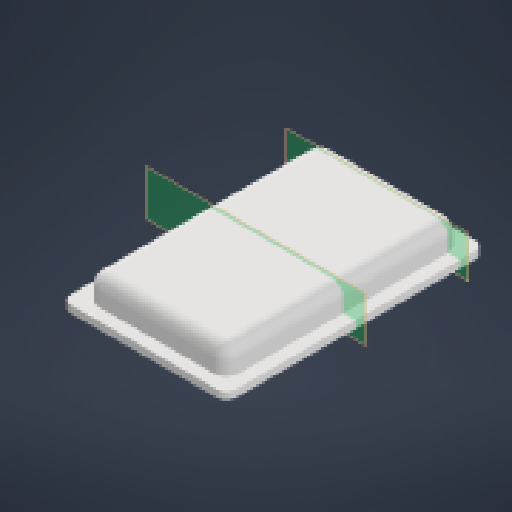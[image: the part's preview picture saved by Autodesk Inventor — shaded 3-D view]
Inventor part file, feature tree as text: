
AUTODESK INVENTOR PART (.ipt)
format: ipt  version: 2024 (Build 280153000, 153)  size: 327,168 bytes
history: native  units: mm
features: reference x17, other x6, extrude x5, sketch x5, fillet x2, chamfer x1, shell x1, mirror x1, projected_geometry x1
ambient origin geometry x8: Origin, YZ Plane, XZ Plane, XY Plane, X Axis, Y Axis, Z Axis, Center Point
bodies: Body1 (feature_tree)
feature tree (39):
  other  "Твердое тело1"
  extrude  "Выдавливание1"  Depth=2.0mm
  chamfer  "Фаска1"  Distance=2.0mm
  extrude  "Выдавливание2"  Depth=1.0mm TaperAngle=45.0deg
  extrude  "Выдавливание3"  Depth=3.0mm TaperAngle=0.0deg
  fillet  "Сопряжение1"  Radius=5.0mm
  other  "РабПлоскость1"
  other  "РабПлоскость2"
  shell  "Оболочка1"  Thickness=10.25mm
  extrude  "Выдавливание5"  Depth=5.0mm
  mirror  "Зеркальное отражение2"
  extrude  "Выдавливание6"  Depth=4.0mm
  fillet  "Сопряжение2"  Radius=4.0mm
  sketch  "Эскиз1"
  reference  "Ссылка1"
  reference  "Ссылка2"
  reference  "Ссылка3"
  reference  "Ссылка4"
  reference  "Ссылка5"
  reference  "Ссылка6"
  reference  "Ссылка7"
  reference  "Ссылка8"
  sketch  "Эскиз2"
  reference  "Ссылка9"
  reference  "Ссылка10"
  reference  "Ссылка11"
  reference  "Ссылка12"
  reference  "Ссылка13"
  reference  "Ссылка15"
  reference  "Ссылка16"
  sketch  "Эскиз3"
  projected_geometry  "Спроецированная петля2"
  sketch  "Эскиз5"
  sketch  "Эскиз6"
  reference  "Ссылка17"
  reference  "Ссылка18"
  parser-record x1  (decoder bookkeeping rows leaked as tree rows — omitted from the tree; the rows remain in map.json)
  other  "back_box_asembly.iam"
  other  "back_box:1"
note: 1 file-system path scrubbed to <path> (originals preserved in map.json)
